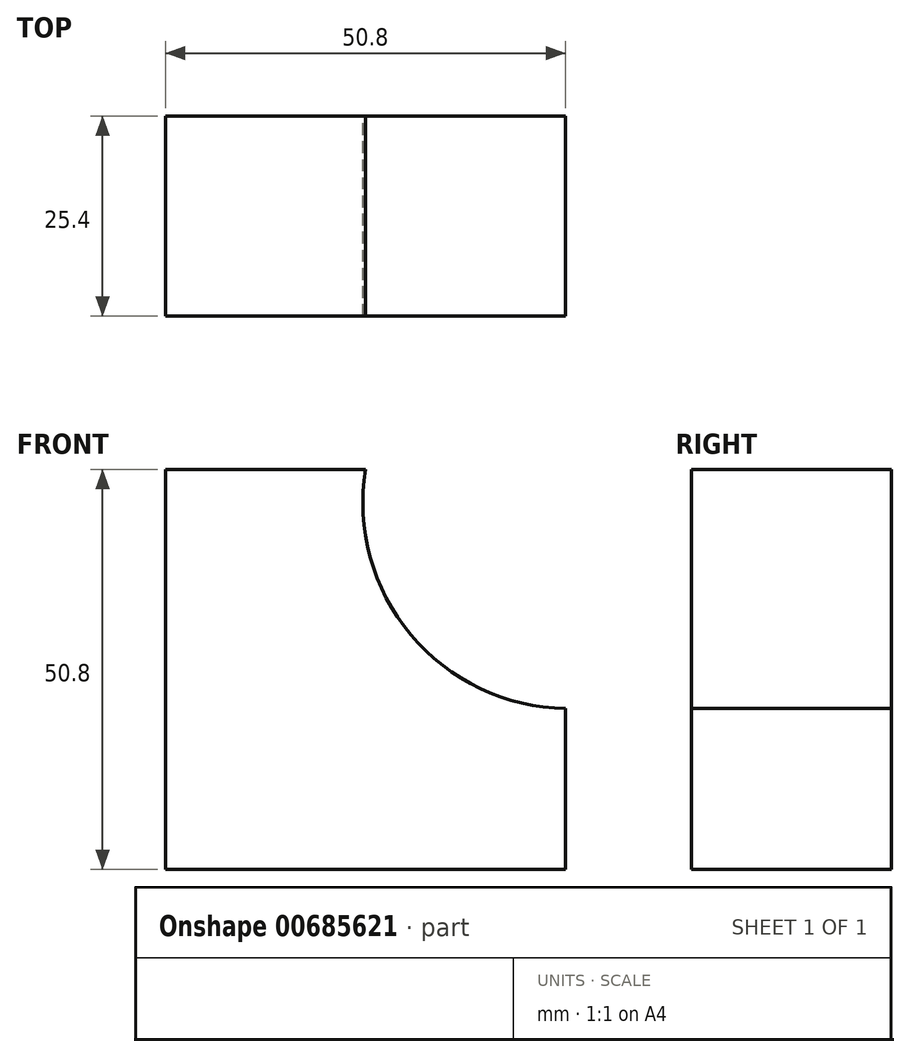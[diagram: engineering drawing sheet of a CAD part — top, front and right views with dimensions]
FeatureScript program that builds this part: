
annotation { "Feature Type Name" : "Feature", "Feature Type Description" : "" }
export const myFeature = defineFeature(function(context is Context, id is Id, definition is map)
    precondition{}
    {
        {
            var Q0;
            Q0=qCreatedBy(makeId("Front.planeOp"),FACE);
            var sketch = newSketch(context, id + "F0", { "sketchPlane" : qUnion([Q0])});
            skLineSegment(sketch, "E0", {"start": v(-58, 50.8) * mm, "end": v(-58, 0) * mm});
            skLineSegment(sketch, "E1", {"start": v(-58, 0) * mm, "end": v(-7.2, 0) * mm});
            skLineSegment(sketch, "E2", {"start": v(-58, 50.8) * mm, "end": v(-32.6, 50.8) * mm});
            skLineSegment(sketch, "E3", {"start": v(-7.2, 0) * mm, "end": v(-7.2, 20.44) * mm});
            skArc(sketch, "E4", {"start": v(-32.6, 50.8) * mm, "mid": v(-26.85, 29.81) * mm, "end": v(-7.2, 20.44) * mm});
            skSolve(sketch);
        }
        {
            var Q0;
            Q0 = qSketchRegion(id + "F0", true);
            extrude(context, id + "F1", {"entities" : qUnion([Q0]), "depth" : 25.4 * mm, "offsetDistance" : 25.4 * mm});
        }
    });
